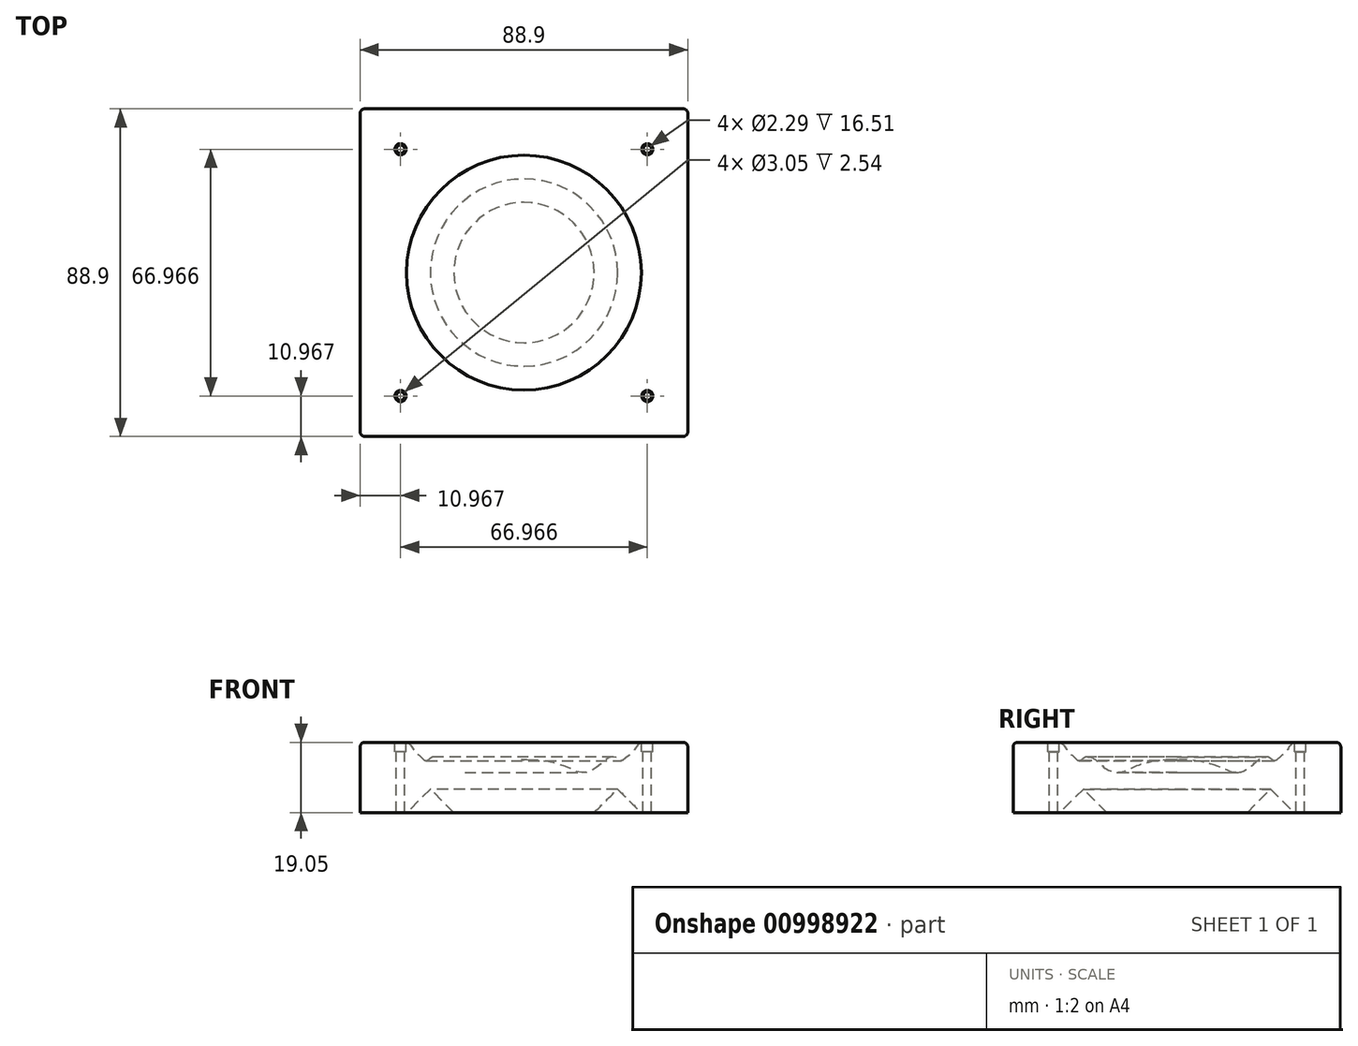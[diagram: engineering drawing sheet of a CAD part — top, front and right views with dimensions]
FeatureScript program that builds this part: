
annotation { "Feature Type Name" : "Feature", "Feature Type Description" : "" }
export const myFeature = defineFeature(function(context is Context, id is Id, definition is map)
    precondition{}
    {
        {
            var Q0;
            Q0=qCreatedBy(makeId("Front.planeOp"),FACE);
            var sketch = newSketch(context, id + "F0", { "sketchPlane" : qUnion([Q0])});
            skLineSegment(sketch, "E0", {"start": v(44.45, 19.05) * mm, "end": v(32.58, 19.05) * mm});
            skFitSpline(sketch, "E1", {"points": [v(31.84, 19.05) * mm, v(29.7, 16.64) * mm, v(28.05, 15.2) * mm, v(26.43, 14.03) * mm, v(25, 14.97) * mm, v(22.63, 14.67) * mm, v(20.05, 12.48) * mm, v(16.23, 10.82) * mm, v(12.74, 11.85) * mm, v(0, 14.34) * mm], "startDerivative": vector(-27.55, -1.97) * mm, "endDerivative": vector(-90.15, -1.67) * mm});
            skLineSegment(sketch, "E2", {"start": v(32.58, 19.05) * mm, "end": v(31.84, 19.05) * mm});
            skLineSegment(sketch, "E3", {"start": v(44.45, 19.05) * mm, "end": v(44.45, 0) * mm});
            skLineSegment(sketch, "E4", {"start": v(0, 14.34) * mm, "end": v(0, 0) * mm});
            skLineSegment(sketch, "E5", {"start": v(0, 0) * mm, "end": v(44.45, 0) * mm});
            skSolve(sketch);
        }
        {
            var Q0;
            Q0=makeQuery(id+"F0.imprint","IMPRINT",FACE,{"disambiguationData":[TD([[makeQuery(id+"F0.imprint","IMPRINT",EDGE,{"derivedFrom":sQuery(id+"F0.wireOp",EDGE,"E0")}),1.0]])]});
            var Q1;
            Q1=sQuery(id+"F0.wireOp",EDGE,"E4");
            revolve(context, id + "F1", {"surfaceOperationType" : NewSurfaceOperationType.NEW, "entities" : qUnion([Q0]), "axis" : qUnion([Q1]), "revolveType" : RevolveType.FULL});
        }
        {
            var Q0;
            Q0=makeQuery(id+"F1.opRevolve","SWEPT_FACE",FACE,{"disambiguationData":[OSD([sQuery(id+"F0.wireOp",EDGE,"E5")])]});
            var sketch = newSketch(context, id + "F2", { "sketchPlane" : qUnion([Q0])});
            skLineSegment(sketch, "E6.bottom", {"start": v(0, 44.45) * mm, "end": v(44.45, 44.45) * mm});
            skLineSegment(sketch, "E6.top", {"start": v(0, 0) * mm, "end": v(44.45, 0) * mm});
            skLineSegment(sketch, "E6.left", {"start": v(0, 44.45) * mm, "end": v(0, 0) * mm});
            skLineSegment(sketch, "E6.right", {"start": v(44.45, 44.45) * mm, "end": v(44.45, 0) * mm});
            skLineSegment(sketch, "E7.bottom", {"start": v(44.45, 44.45) * mm, "end": v(-44.45, 44.45) * mm});
            skLineSegment(sketch, "E7.top", {"start": v(44.45, -44.45) * mm, "end": v(-44.45, -44.45) * mm});
            skLineSegment(sketch, "E7.left", {"start": v(44.45, 44.45) * mm, "end": v(44.45, -44.45) * mm});
            skLineSegment(sketch, "E7.right", {"start": v(-44.45, 44.45) * mm, "end": v(-44.45, -44.45) * mm});
            skCircle(sketch, "E8.0", {"center": v(0, 0) * mm, "radius": 40.48 * mm});
            skSolve(sketch);
        }
        {
            var Q0;
            {var subQ0=sQuery(id+"F2.wireOp",EDGE,"E7.right");var subQ1=sQuery(id+"F2.wireOp",EDGE,"E7.top");var subQ2=makeQuery(id+"F2.imprint","INTERSECT",VERTEX,{"derivedFrom":[subQ1,subQ0]});Q0=makeQuery(id+"F2.imprint","IMPRINT",FACE,{"disambiguationData":[TD([[makeQuery(id+"F2.imprint","IMPRINT",EDGE,{"disambiguationData":[TD([[subQ2,1.0]])],"derivedFrom":subQ1}),-1.0]])]});}
            var Q1;
            {var subQ0=sQuery(id+"F2.wireOp",EDGE,"E7.left");Q1=makeQuery(id+"F2.imprint","IMPRINT",FACE,{"disambiguationData":[TD([[makeQuery(id+"F2.imprint","IMPRINT",EDGE,{"derivedFrom":subQ0}),-1.0]])]});}
            var Q2;
            {var subQ0=sQuery(id+"F2.wireOp",EDGE,"E6.bottom");Q2=makeQuery(id+"F2.imprint","IMPRINT",FACE,{"disambiguationData":[TD([[makeQuery(id+"F2.imprint","IMPRINT",EDGE,{"derivedFrom":subQ0}),-1.0]])]});}
            var Q3;
            {var subQ0=sQuery(id+"F2.wireOp",EDGE,"E7.bottom");Q3=makeQuery(id+"F2.imprint","IMPRINT",FACE,{"disambiguationData":[TD([[makeQuery(id+"F2.imprint","IMPRINT",EDGE,{"derivedFrom":subQ0}),1.0]])]});}
            var Q4;
            Q4=makeQuery(id+"F1.opRevolve","SWEPT_FACE",FACE,{"disambiguationData":[OSD([sQuery(id+"F0.wireOp",EDGE,"E0"),sQuery(id+"F0.wireOp",EDGE,"E2")])]});
            extrude(context, id + "F3", {"entities" : qUnion([Q0, Q1, Q2, Q3]), "operationType" : NewBodyOperationType.ADD, "endBound" : BoundingType.UP_TO_SURFACE, "oppositeDirection" : true, "depth" : 25.4 * mm, "endBoundEntityFace" : qUnion([Q4]), "offsetDistance" : 25.4 * mm});
        }
        {
            var Q0;
            {var subQ0=sQuery(id+"F2.wireOp",EDGE,"E7.top");Q0=makeQuery(id+"F3.boolean.opBoolean","MERGE",EDGE,{"derivedFrom":[makeQuery(id+"F3.opExtrude","CAP_EDGE",EDGE,{"disambiguationData":[OSD([subQ0]),TDD([makeQuery(id+"F2.imprint","IMPRINT",EDGE,{"disambiguationData":[TD([[makeQuery(id+"F2.imprint","INTERSECT",VERTEX,{"derivedFrom":[subQ0,sQuery(id+"F2.wireOp",EDGE,"E7.left")]}),-1.0]])],"derivedFrom":subQ0})])],"isStart":false}),makeQuery(id+"F3.opExtrude","CAP_EDGE",EDGE,{"disambiguationData":[OSD([subQ0]),TDD([makeQuery(id+"F2.imprint","IMPRINT",EDGE,{"disambiguationData":[TD([[makeQuery(id+"F2.imprint","INTERSECT",VERTEX,{"derivedFrom":[subQ0,sQuery(id+"F2.wireOp",EDGE,"E7.right")]}),1.0]])],"derivedFrom":subQ0})])],"isStart":false})]});}
            var Q1;
            Q1=makeQuery(id+"F3.boolean.opBoolean","MERGE",EDGE,{"derivedFrom":[makeQuery(id+"F3.opExtrude","CAP_EDGE",EDGE,{"disambiguationData":[OSD([sQuery(id+"F2.wireOp",EDGE,"E6.right")])],"isStart":false}),makeQuery(id+"F3.opExtrude","CAP_EDGE",EDGE,{"disambiguationData":[OSD([sQuery(id+"F2.wireOp",EDGE,"E7.left")])],"isStart":false})]});
            var Q2;
            Q2=makeQuery(id+"F3.opExtrude","SWEPT_EDGE",EDGE,{"disambiguationData":[OSD([sQuery(id+"F2.wireOp",EDGE,"E7.top"),sQuery(id+"F2.wireOp",EDGE,"E7.left")])]});
            var Q3;
            Q3=makeQuery(id+"F3.opExtrude","SWEPT_EDGE",EDGE,{"disambiguationData":[OSD([sQuery(id+"F2.wireOp",EDGE,"E6.bottom"),sQuery(id+"F2.wireOp",EDGE,"E6.right")])]});
            var Q4;
            Q4=makeQuery(id+"F3.boolean.opBoolean","MERGE",EDGE,{"derivedFrom":[makeQuery(id+"F3.opExtrude","CAP_EDGE",EDGE,{"disambiguationData":[OSD([sQuery(id+"F2.wireOp",EDGE,"E6.bottom")])],"isStart":false}),makeQuery(id+"F3.opExtrude","CAP_EDGE",EDGE,{"disambiguationData":[OSD([sQuery(id+"F2.wireOp",EDGE,"E7.bottom")])],"isStart":false})]});
            var Q5;
            {var subQ0=sQuery(id+"F2.wireOp",EDGE,"E7.right");Q5=makeQuery(id+"F3.boolean.opBoolean","MERGE",EDGE,{"derivedFrom":[makeQuery(id+"F3.opExtrude","CAP_EDGE",EDGE,{"disambiguationData":[OSD([subQ0]),TDD([makeQuery(id+"F2.imprint","IMPRINT",EDGE,{"disambiguationData":[TD([[makeQuery(id+"F2.imprint","INTERSECT",VERTEX,{"derivedFrom":[sQuery(id+"F2.wireOp",EDGE,"E7.bottom"),subQ0]}),-1.0]])],"derivedFrom":subQ0})])],"isStart":false}),makeQuery(id+"F3.opExtrude","CAP_EDGE",EDGE,{"disambiguationData":[OSD([subQ0]),TDD([makeQuery(id+"F2.imprint","IMPRINT",EDGE,{"disambiguationData":[TD([[makeQuery(id+"F2.imprint","INTERSECT",VERTEX,{"derivedFrom":[sQuery(id+"F2.wireOp",EDGE,"E7.top"),subQ0]}),1.0]])],"derivedFrom":subQ0})])],"isStart":false})]});}
            var Q6;
            Q6=makeQuery(id+"F3.opExtrude","SWEPT_EDGE",EDGE,{"disambiguationData":[OSD([sQuery(id+"F2.wireOp",EDGE,"E7.top"),sQuery(id+"F2.wireOp",EDGE,"E7.right")])]});
            var Q7;
            Q7=makeQuery(id+"F3.opExtrude","SWEPT_EDGE",EDGE,{"disambiguationData":[OSD([sQuery(id+"F2.wireOp",EDGE,"E7.bottom"),sQuery(id+"F2.wireOp",EDGE,"E7.right")])]});
            fillet(context, id + "F4", {"entities" : qUnion([Q0, Q1, Q2, Q3, Q4, Q5, Q6, Q7]), "radius" : 1.27 * mm, "tangentPropagation" : true, "allowEdgeOverflow" : false});
        }
        {
            var Q0;
            {var subQ0=sQuery(id+"F2.wireOp",EDGE,"E7.right");var subQ1=sQuery(id+"F2.wireOp",EDGE,"E7.top");var subQ2=sQuery(id+"F0.wireOp",EDGE,"E5");var subQ3=sQuery(id+"F0.wireOp",EDGE,"E3");Q0=makeQuery(id+"F3.boolean.opBoolean","MERGE",FACE,{"derivedFrom":[makeQuery(id+"F1.opRevolve","SWEPT_FACE",FACE,{"disambiguationData":[OSD([sQuery(id+"F0.wireOp",EDGE,"E0"),sQuery(id+"F0.wireOp",EDGE,"E2")])]}),makeQuery(id+"F3.opExtrude","CAP_FACE",FACE,{"disambiguationData":[OSD([subQ3,subQ2,sQuery(id+"F2.wireOp",EDGE,"E6.bottom"),sQuery(id+"F2.wireOp",EDGE,"E6.right")])],"isStart":false}),makeQuery(id+"F3.opExtrude","CAP_FACE",FACE,{"disambiguationData":[OSD([subQ3,subQ2,sQuery(id+"F2.wireOp",EDGE,"E7.bottom"),subQ0])],"isStart":false}),makeQuery(id+"F3.opExtrude","CAP_FACE",FACE,{"disambiguationData":[OSD([subQ3,subQ2,subQ1,sQuery(id+"F2.wireOp",EDGE,"E7.left")])],"isStart":false}),makeQuery(id+"F3.opExtrude","CAP_FACE",FACE,{"disambiguationData":[OSD([subQ3,subQ2,subQ1,subQ0])],"isStart":false})]});}
            var sketch = newSketch(context, id + "F5", { "sketchPlane" : qUnion([Q0])});
            skCircle(sketch, "E9.0", {"center": v(0, 0) * mm, "radius": 31.84 * mm});
            skCircle(sketch, "E10", {"center": v(-33.48, 33.48) * mm, "radius": 1.14 * mm});
            skCircle(sketch, "E11", {"center": v(-33.48, 33.48) * mm, "radius": 1.52 * mm});
            skCircle(sketch, "E12", {"center": v(33.48, 33.48) * mm, "radius": 1.14 * mm});
            skCircle(sketch, "E13", {"center": v(33.48, 33.48) * mm, "radius": 1.52 * mm});
            skCircle(sketch, "E14", {"center": v(-33.48, -33.48) * mm, "radius": 1.14 * mm});
            skCircle(sketch, "E15", {"center": v(-33.48, -33.48) * mm, "radius": 1.52 * mm});
            skCircle(sketch, "E16", {"center": v(33.48, -33.48) * mm, "radius": 1.14 * mm});
            skCircle(sketch, "E17", {"center": v(33.48, -33.48) * mm, "radius": 1.52 * mm});
            skSolve(sketch);
        }
        {
            var Q0;
            Q0=makeQuery(id+"F5.imprint","IMPRINT",FACE,{"disambiguationData":[TD([[makeQuery(id+"F5.imprint","IMPRINT",EDGE,{"derivedFrom":sQuery(id+"F5.wireOp",EDGE,"E10")}),1.0]])]});
            var Q1;
            Q1=makeQuery(id+"F5.imprint","IMPRINT",FACE,{"disambiguationData":[TD([[makeQuery(id+"F5.imprint","IMPRINT",EDGE,{"derivedFrom":sQuery(id+"F5.wireOp",EDGE,"E14")}),1.0]])]});
            var Q2;
            Q2=makeQuery(id+"F5.imprint","IMPRINT",FACE,{"disambiguationData":[TD([[makeQuery(id+"F5.imprint","IMPRINT",EDGE,{"derivedFrom":sQuery(id+"F5.wireOp",EDGE,"E16")}),1.0]])]});
            var Q3;
            Q3=makeQuery(id+"F5.imprint","IMPRINT",FACE,{"disambiguationData":[TD([[makeQuery(id+"F5.imprint","IMPRINT",EDGE,{"derivedFrom":sQuery(id+"F5.wireOp",EDGE,"E12")}),1.0]])]});
            extrude(context, id + "F6", {"entities" : qUnion([Q0, Q1, Q2, Q3]), "operationType" : NewBodyOperationType.REMOVE, "endBound" : BoundingType.THROUGH_ALL, "oppositeDirection" : true, "depth" : 25.4 * mm, "offsetDistance" : 25.4 * mm});
        }
        {
            var Q0;
            Q0=makeQuery(id+"F5.imprint","IMPRINT",FACE,{"disambiguationData":[TD([[makeQuery(id+"F5.imprint","IMPRINT",EDGE,{"derivedFrom":sQuery(id+"F5.wireOp",EDGE,"E10")}),-1.0]])]});
            var Q1;
            Q1=makeQuery(id+"F5.imprint","IMPRINT",FACE,{"disambiguationData":[TD([[makeQuery(id+"F5.imprint","IMPRINT",EDGE,{"derivedFrom":sQuery(id+"F5.wireOp",EDGE,"E12")}),-1.0]])]});
            var Q2;
            Q2=makeQuery(id+"F5.imprint","IMPRINT",FACE,{"disambiguationData":[TD([[makeQuery(id+"F5.imprint","IMPRINT",EDGE,{"derivedFrom":sQuery(id+"F5.wireOp",EDGE,"E16")}),-1.0]])]});
            var Q3;
            Q3=makeQuery(id+"F5.imprint","IMPRINT",FACE,{"disambiguationData":[TD([[makeQuery(id+"F5.imprint","IMPRINT",EDGE,{"derivedFrom":sQuery(id+"F5.wireOp",EDGE,"E14")}),-1.0]])]});
            extrude(context, id + "F7", {"entities" : qUnion([Q0, Q1, Q2, Q3]), "operationType" : NewBodyOperationType.REMOVE, "oppositeDirection" : true, "depth" : 2.54 * mm, "offsetDistance" : 25.4 * mm});
        }
        {
            var Q0;
            Q0=qCreatedBy(makeId("Right.planeOp"),FACE);
            var sketch = newSketch(context, id + "F8", { "sketchPlane" : qUnion([Q0])});
            skLineSegment(sketch, "E18", {"start": v(0, 0) * mm, "end": v(0, 6.35) * mm});
            skLineSegment(sketch, "E19", {"start": v(-25.4, 0) * mm, "end": v(-19.05, 0) * mm});
            skLineSegment(sketch, "E20", {"start": v(-19.05, 0) * mm, "end": v(-25.4, 6.35) * mm});
            skLineSegment(sketch, "E21", {"start": v(-25.4, 0) * mm, "end": v(-31.75, 0) * mm});
            skLineSegment(sketch, "E22", {"start": v(-31.75, 0) * mm, "end": v(-25.4, 6.35) * mm});
            skSolve(sketch);
        }
        {
            var Q0;
            Q0 = qSketchRegion(id + "F8", true);
            var Q1;
            Q1=sQuery(id+"F8.wireOp",EDGE,"E18");
            revolve(context, id + "F9", {"operationType" : NewBodyOperationType.REMOVE, "surfaceOperationType" : NewSurfaceOperationType.NEW, "entities" : qUnion([Q0]), "axis" : qUnion([Q1]), "revolveType" : RevolveType.FULL, "oppositeDirection" : true});
        }
    });
